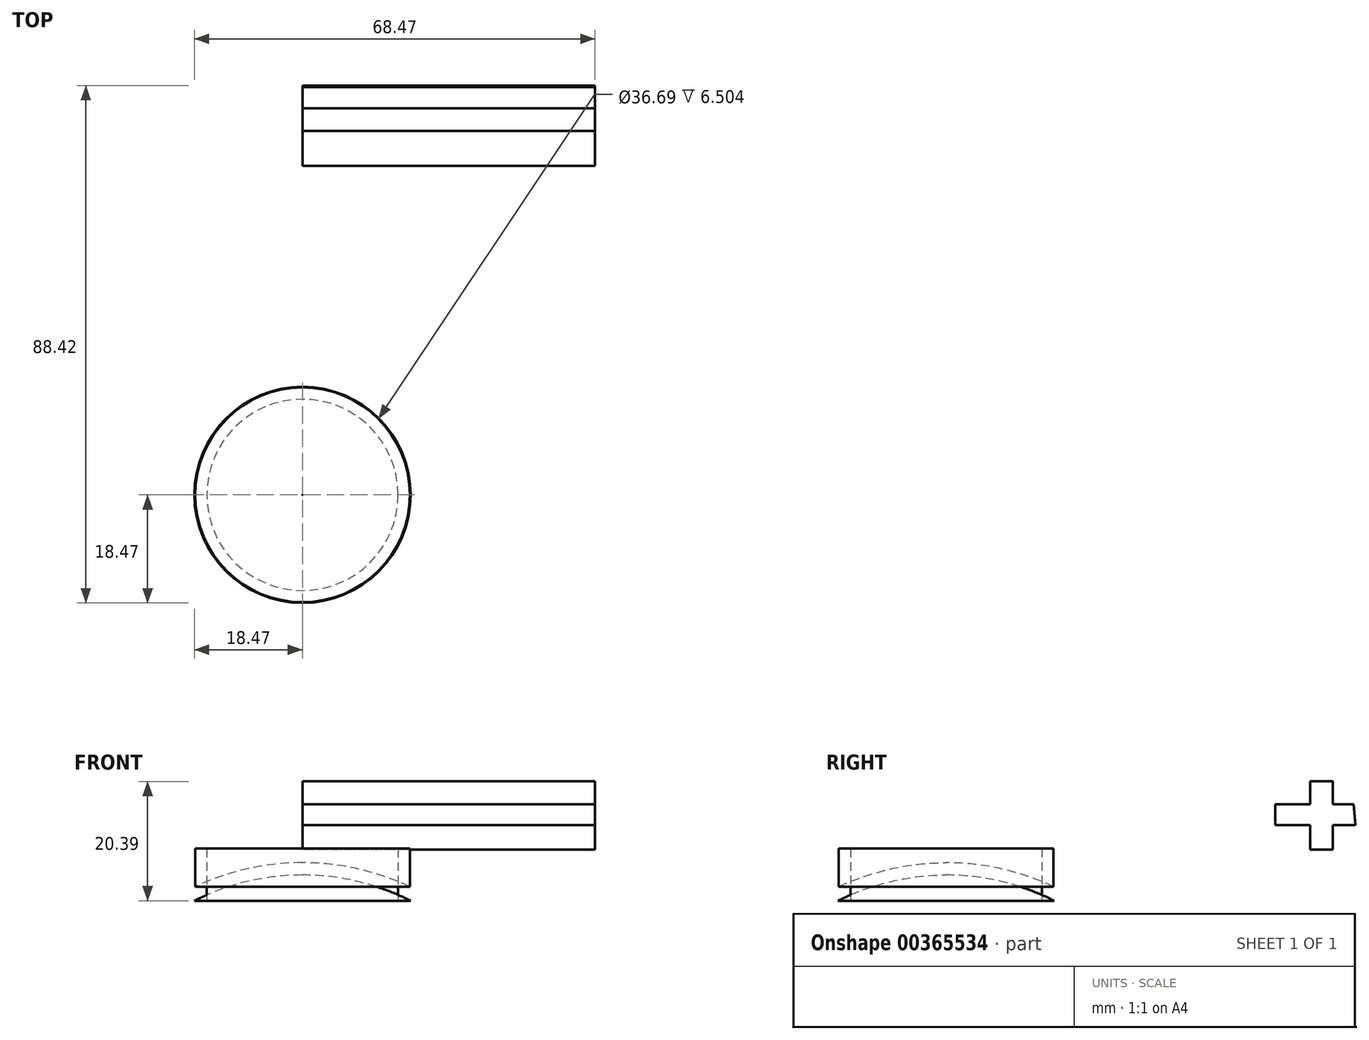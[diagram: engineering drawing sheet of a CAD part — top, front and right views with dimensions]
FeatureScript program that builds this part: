
annotation { "Feature Type Name" : "Feature", "Feature Type Description" : "" }
export const myFeature = defineFeature(function(context is Context, id is Id, definition is map)
    precondition{}
    {
        {
            var Q0;
            Q0=qCreatedBy(makeId("Right.planeOp"),FACE);
            var sketch = newSketch(context, id + "F0", { "sketchPlane" : qUnion([Q0])});
            skArc(sketch, "E0", {"start": v(-18.35, 30.63) * mm, "mid": v(-42.03, -17.74) * mm, "end": v(0, -51.4) * mm});
            skArc(sketch, "E1.0", {"start": v(-18.47, 28.23) * mm, "mid": v(-39.86, -17.83) * mm, "end": v(0, -49.3) * mm});
            skLineSegment(sketch, "E2", {"start": v(-18.47, 28.23) * mm, "end": v(-16.35, 28.23) * mm});
            skLineSegment(sketch, "E3", {"start": v(-16.35, 28.23) * mm, "end": v(-16.35, 37.13) * mm});
            skLineSegment(sketch, "E4", {"start": v(-16.35, 37.13) * mm, "end": v(-18.35, 37.13) * mm});
            skLineSegment(sketch, "E5", {"start": v(-18.35, 37.13) * mm, "end": v(-18.35, 30.63) * mm});
            skLineSegment(sketch, "E6", {"start": v(0, -49.3) * mm, "end": v(0, -51.4) * mm});
            skSolve(sketch);
        }
        {
            var Q0;
            Q0=qCreatedBy(makeId("Right.planeOp"),FACE);
            var sketch = newSketch(context, id + "F1", { "sketchPlane" : qUnion([Q0])});
            skLineSegment(sketch, "E7", {"start": v(0, -62.43) * mm, "end": v(0, 50.7) * mm});
            skSolve(sketch);
        }
        {
            var Q0;
            Q0 = qSketchRegion(id + "F0", true);
            var Q1;
            Q1=sQuery(id+"F0.wireOp",EDGE,"E0");
            var Q2;
            Q2=sQuery(id+"F0.wireOp",EDGE,"E1.0");
            var Q3;
            Q3=sQuery(id+"F0.wireOp",EDGE,"E5");
            var Q4;
            Q4=sQuery(id+"F0.wireOp",EDGE,"E3");
            var Q5;
            Q5=sQuery(id+"F0.wireOp",EDGE,"E2");
            var Q6;
            Q6=sQuery(id+"F0.wireOp",EDGE,"E4");
            var Q7;
            Q7=sQuery(id+"F1.wireOp",EDGE,"E7");
            revolve(context, id + "F2", {"entities" : qUnion([Q0]), "surfaceEntities" : qUnion([Q1, Q2, Q3, Q4, Q5, Q6]), "axis" : qUnion([Q7]), "revolveType" : RevolveType.FULL});
        }
        {
            var Q0;
            Q0=qCreatedBy(makeId("Right.planeOp"),FACE);
            var sketch = newSketch(context, id + "F3", { "sketchPlane" : qUnion([Q0])});
            skLineSegment(sketch, "E8", {"start": v(69.65, 44.74) * mm, "end": v(66.07, 44.74) * mm});
            skLineSegment(sketch, "E9", {"start": v(66.07, 44.74) * mm, "end": v(66.07, 48.62) * mm});
            skLineSegment(sketch, "E10", {"start": v(66.07, 48.62) * mm, "end": v(62.2, 48.62) * mm});
            skLineSegment(sketch, "E11", {"start": v(62.2, 48.62) * mm, "end": v(62.2, 44.74) * mm});
            skLineSegment(sketch, "E12", {"start": v(62.2, 44.74) * mm, "end": v(56.23, 44.74) * mm});
            skLineSegment(sketch, "E13", {"start": v(56.23, 44.74) * mm, "end": v(56.23, 41.16) * mm});
            skLineSegment(sketch, "E14", {"start": v(56.23, 41.16) * mm, "end": v(62.2, 41.16) * mm});
            skLineSegment(sketch, "E15", {"start": v(62.2, 41.16) * mm, "end": v(62.2, 36.99) * mm});
            skLineSegment(sketch, "E16", {"start": v(62.2, 36.99) * mm, "end": v(66.07, 36.99) * mm});
            skLineSegment(sketch, "E17", {"start": v(66.07, 36.99) * mm, "end": v(66.07, 41.16) * mm});
            skLineSegment(sketch, "E18", {"start": v(66.07, 41.16) * mm, "end": v(69.95, 41.16) * mm});
            skLineSegment(sketch, "E19", {"start": v(69.95, 41.16) * mm, "end": v(69.65, 44.74) * mm});
            skSolve(sketch);
        }
        {
            var Q0;
            Q0=makeQuery(id+"F3.imprint","IMPRINT",FACE,{"disambiguationData":[TD([[makeQuery(id+"F3.imprint","IMPRINT",EDGE,{"derivedFrom":sQuery(id+"F3.wireOp",EDGE,"E8")}),1.0]])]});
            extrude(context, id + "F4", {"entities" : qUnion([Q0]), "depth" : 50 * mm});
        }
    });
